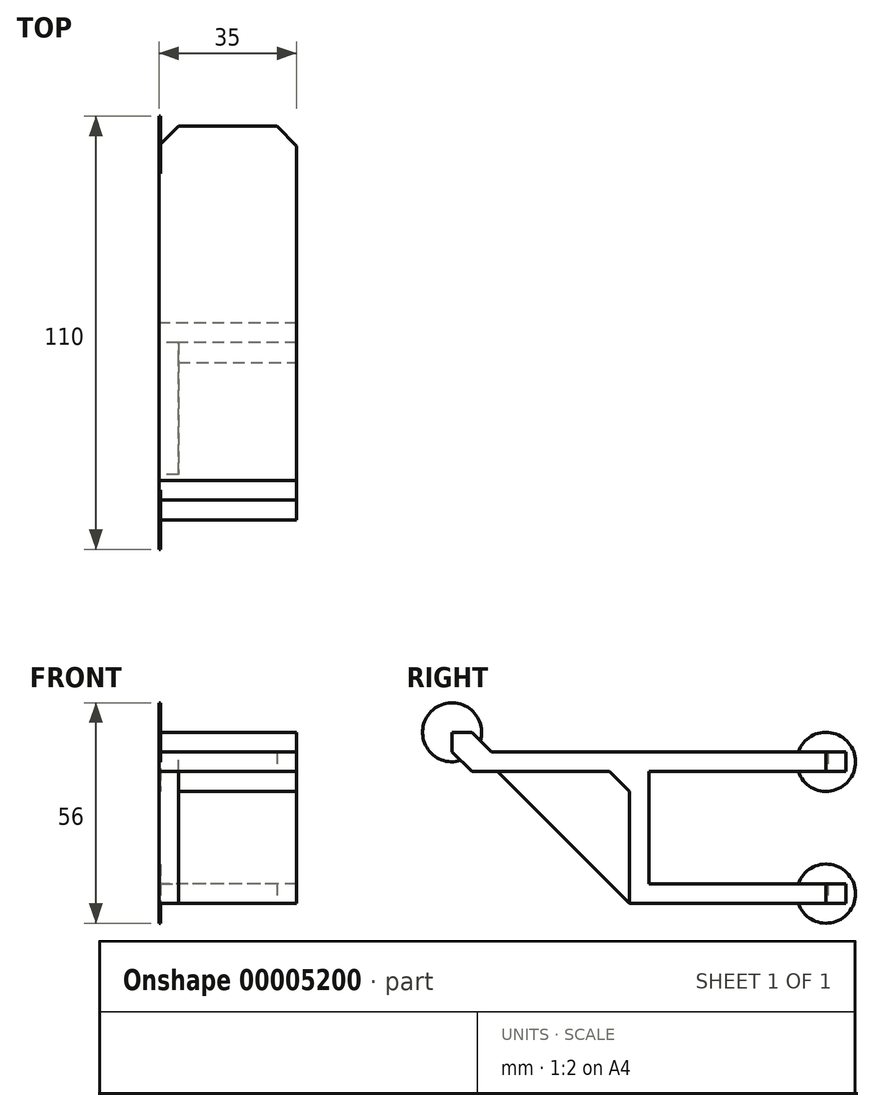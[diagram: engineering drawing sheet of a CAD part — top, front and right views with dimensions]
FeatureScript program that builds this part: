
annotation { "Feature Type Name" : "Feature", "Feature Type Description" : "" }
export const myFeature = defineFeature(function(context is Context, id is Id, definition is map)
    precondition{}
    {
        {
            var Q0;
            Q0=qCreatedBy(makeId("Right.planeOp"),FACE);
            var sketch = newSketch(context, id + "F0", { "sketchPlane" : qUnion([Q0])});
            skLineSegment(sketch, "E0.bottom", {"start": v(25, 14.25) * mm, "end": v(-25, 14.25) * mm});
            skLineSegment(sketch, "E0.top", {"start": v(25, -14.25) * mm, "end": v(-25, -14.25) * mm});
            skLineSegment(sketch, "E0.left", {"start": v(25, 14.25) * mm, "end": v(25, -14.25) * mm, "construction": true});
            skLineSegment(sketch, "E0.right", {"start": v(-25, 14.25) * mm, "end": v(-25, -14.25) * mm});
            skPoint(sketch, "E0.middle", {"position": v(0, 0) * mm});
            skLineSegment(sketch, "E1", {"start": v(25, 14.25) * mm, "end": v(25, 19.25) * mm});
            skLineSegment(sketch, "E2", {"start": v(25, 19.25) * mm, "end": v(-65, 19.25) * mm});
            skLineSegment(sketch, "E3", {"start": v(-65, 19.25) * mm, "end": v(-70, 24.25) * mm});
            skLineSegment(sketch, "E4", {"start": v(-70, 24.25) * mm, "end": v(-75, 24.25) * mm});
            skLineSegment(sketch, "E5", {"start": v(-30, -19.25) * mm, "end": v(25, -19.25) * mm});
            skLineSegment(sketch, "E6", {"start": v(25, -19.25) * mm, "end": v(25, -14.25) * mm});
            skLineSegment(sketch, "E7", {"start": v(-75, 24.25) * mm, "end": v(-75, 14.25) * mm});
            skLineSegment(sketch, "E8", {"start": v(-75, 14.25) * mm, "end": v(-30, 14.25) * mm});
            skLineSegment(sketch, "E9", {"start": v(-30, 14.25) * mm, "end": v(-30, -19.25) * mm});
            skLineSegment(sketch, "E10", {"start": v(-25, 14.25) * mm, "end": v(-30, 14.25) * mm, "construction": true});
            skSolve(sketch);
        }
        {
            var Q0;
            Q0 = qSketchRegion(id + "F0", true);
            extrude(context, id + "F1", {"entities" : qUnion([Q0]), "depth" : 35 * mm, "symmetric" : true});
        }
        {
            var Q0;
            Q0=makeQuery(id+"F1.opExtrude","CAP_FACE",FACE,{"disambiguationData":[OSD([sQuery(id+"F0.wireOp",EDGE,"E0.bottom"),sQuery(id+"F0.wireOp",EDGE,"E0.top"),sQuery(id+"F0.wireOp",EDGE,"E0.right"),sQuery(id+"F0.wireOp",EDGE,"E1"),sQuery(id+"F0.wireOp",EDGE,"E2"),sQuery(id+"F0.wireOp",EDGE,"E3"),sQuery(id+"F0.wireOp",EDGE,"E4"),sQuery(id+"F0.wireOp",EDGE,"E5"),sQuery(id+"F0.wireOp",EDGE,"E6"),sQuery(id+"F0.wireOp",EDGE,"E7"),sQuery(id+"F0.wireOp",EDGE,"E8"),sQuery(id+"F0.wireOp",EDGE,"E9")])],"isStart":true});
            var sketch = newSketch(context, id + "F2", { "sketchPlane" : qUnion([Q0])});
            skLineSegment(sketch, "E11", {"start": v(30, -19.25) * mm, "end": v(63.5, 14.25) * mm});
            skLineSegment(sketch, "E12.0", {"start": v(30, 14.25) * mm, "end": v(30, -19.25) * mm});
            skLineSegment(sketch, "E13", {"start": v(30, 14.25) * mm, "end": v(63.5, 14.25) * mm});
            skSolve(sketch);
        }
        {
            var Q0;
            Q0 = qSketchRegion(id + "F2", true);
            extrude(context, id + "F3", {"entities" : qUnion([Q0]), "operationType" : NewBodyOperationType.ADD, "oppositeDirection" : true, "depth" : 5 * mm});
        }
        {
            var Q0;
            Q0=makeQuery(id+"F1.opExtrude","CAP_EDGE",EDGE,{"disambiguationData":[OSD([sQuery(id+"F0.wireOp",EDGE,"E1")])],"isStart":false});
            var Q1;
            Q1=makeQuery(id+"F1.opExtrude","CAP_EDGE",EDGE,{"disambiguationData":[OSD([sQuery(id+"F0.wireOp",EDGE,"E1")])],"isStart":true});
            var Q2;
            Q2=makeQuery(id+"F1.opExtrude","CAP_EDGE",EDGE,{"disambiguationData":[OSD([sQuery(id+"F0.wireOp",EDGE,"E6")])],"isStart":false});
            var Q3;
            Q3=makeQuery(id+"F1.opExtrude","CAP_EDGE",EDGE,{"disambiguationData":[OSD([sQuery(id+"F0.wireOp",EDGE,"E6")])],"isStart":true});
            var Q4;
            Q4=makeQuery(id+"F1.opExtrude","SWEPT_EDGE",EDGE,{"disambiguationData":[OSD([sQuery(id+"F0.wireOp",EDGE,"E8"),sQuery(id+"F0.wireOp",EDGE,"E9")])]});
            var Q5;
            Q5=makeQuery(id+"F1.opExtrude","SWEPT_EDGE",EDGE,{"disambiguationData":[OSD([sQuery(id+"F0.wireOp",EDGE,"E7"),sQuery(id+"F0.wireOp",EDGE,"E8")])]});
            chamfer(context, id + "F4", {"entities" : qUnion([Q0, Q1, Q2, Q3, Q4, Q5]), "width" : 5 * mm, "tangentPropagation" : true});
        }
        {
            var Q0;
            Q0=makeQuery(id+"F3.boolean.opBoolean","MERGE",FACE,{"derivedFrom":[makeQuery(id+"F1.opExtrude","CAP_FACE",FACE,{"disambiguationData":[OSD([sQuery(id+"F0.wireOp",EDGE,"E0.bottom"),sQuery(id+"F0.wireOp",EDGE,"E0.top"),sQuery(id+"F0.wireOp",EDGE,"E0.right"),sQuery(id+"F0.wireOp",EDGE,"E1"),sQuery(id+"F0.wireOp",EDGE,"E2"),sQuery(id+"F0.wireOp",EDGE,"E3"),sQuery(id+"F0.wireOp",EDGE,"E4"),sQuery(id+"F0.wireOp",EDGE,"E5"),sQuery(id+"F0.wireOp",EDGE,"E6"),sQuery(id+"F0.wireOp",EDGE,"E7"),sQuery(id+"F0.wireOp",EDGE,"E8"),sQuery(id+"F0.wireOp",EDGE,"E9")])],"isStart":true}),makeQuery(id+"F3.opExtrude","CAP_FACE",FACE,{"disambiguationData":[OSD([sQuery(id+"F2.wireOp",EDGE,"E11"),sQuery(id+"F2.wireOp",EDGE,"E12.0"),sQuery(id+"F2.wireOp",EDGE,"E13")])],"isStart":true})]});
            var sketch = newSketch(context, id + "F5", { "sketchPlane" : qUnion([Q0])});
            skCircle(sketch, "E14", {"center": v(-20, -16.75) * mm, "radius": 7.5 * mm});
            skCircle(sketch, "E15", {"center": v(-20, 16.75) * mm, "radius": 7.5 * mm});
            skCircle(sketch, "E16", {"center": v(75, 24.25) * mm, "radius": 7.5 * mm});
            skSolve(sketch);
        }
        {
            var Q0;
            Q0 = qSketchRegion(id + "F5", true);
            extrude(context, id + "F6", {"entities" : qUnion([Q0]), "operationType" : NewBodyOperationType.ADD, "oppositeDirection" : true, "depth" : 0.5 * mm});
        }
    });
